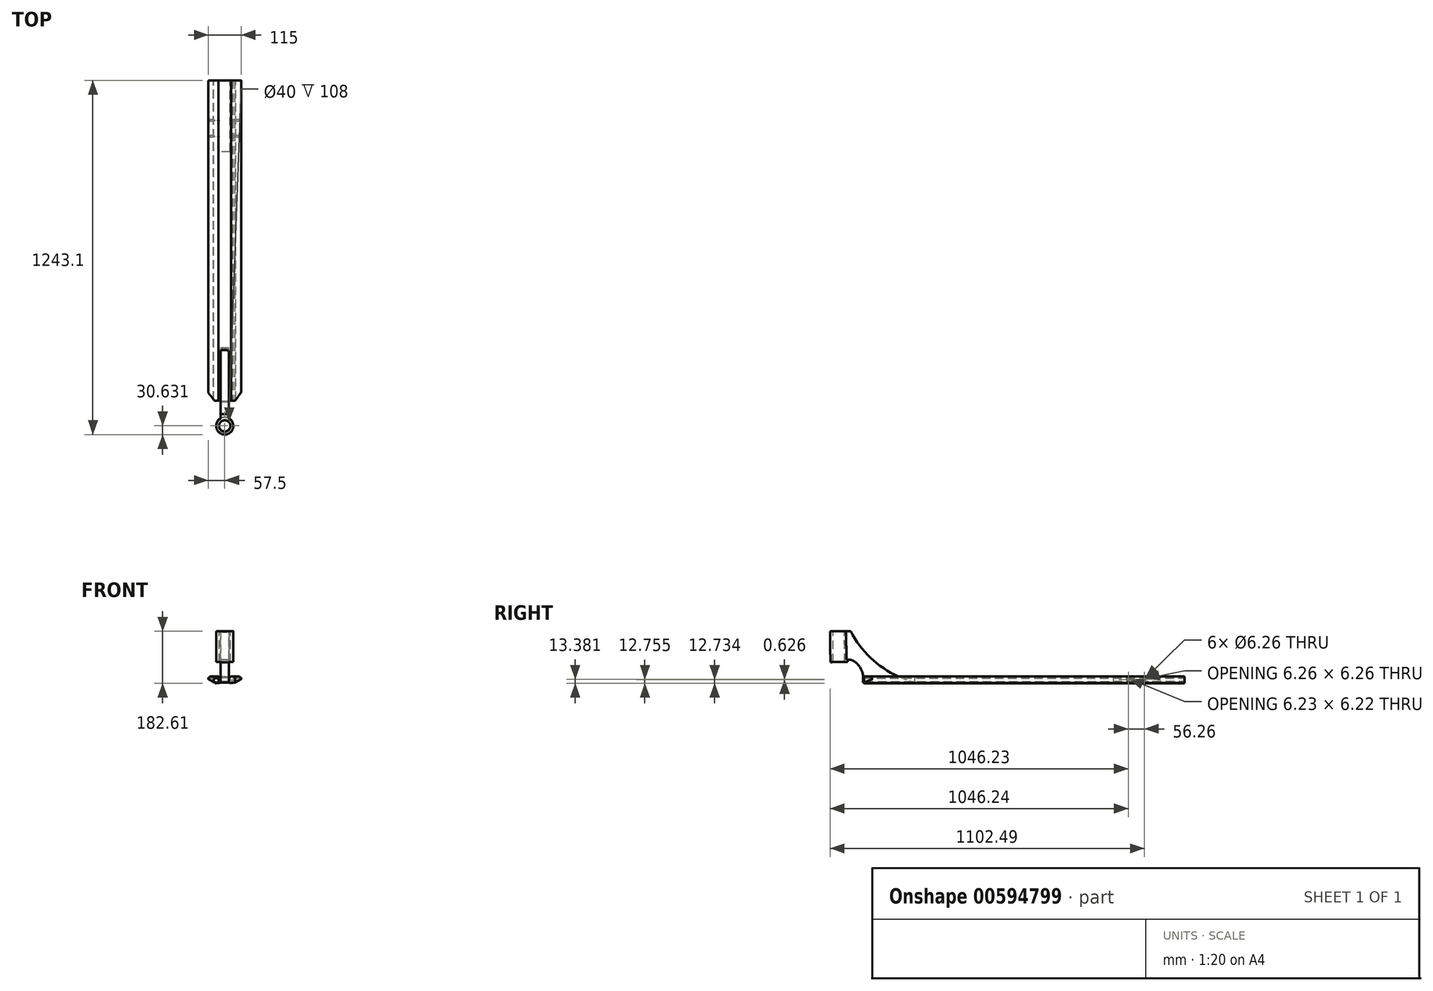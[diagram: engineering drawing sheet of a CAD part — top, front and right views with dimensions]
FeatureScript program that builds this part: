
annotation { "Feature Type Name" : "Feature", "Feature Type Description" : "" }
export const myFeature = defineFeature(function(context is Context, id is Id, definition is map)
    precondition{}
    {
        {
            var Q0;
            Q0=qCreatedBy(makeId("Front.planeOp"),FACE);
            var sketch = newSketch(context, id + "F0", { "sketchPlane" : qUnion([Q0])});
            skLineSegment(sketch, "E0", {"start": v(0, 0) * mm, "end": v(0, 33.47) * mm, "construction": true});
            skLineSegment(sketch, "E1", {"start": v(0, 25.6) * mm, "end": v(22.5, 25.6) * mm});
            skLineSegment(sketch, "E2", {"start": v(22.5, 25.6) * mm, "end": v(22.5, 26.9) * mm});
            skLineSegment(sketch, "E3", {"start": v(22.5, 26.9) * mm, "end": v(51.16, 26.9) * mm});
            skLineSegment(sketch, "E4", {"start": v(57.5, 21.58) * mm, "end": v(51.16, 26.9) * mm});
            skLineSegment(sketch, "E5", {"start": v(57.5, 21.58) * mm, "end": v(57.5, 17.58) * mm});
            skLineSegment(sketch, "E6", {"start": v(57.5, 17.58) * mm, "end": v(32.08, 2.9) * mm});
            skLineSegment(sketch, "E7.MirrorCS", {"start": v(0, 25.6) * mm, "end": v(-22.5, 25.6) * mm});
            skLineSegment(sketch, "E8.MirrorCS", {"start": v(-22.5, 25.6) * mm, "end": v(-22.5, 26.9) * mm});
            skLineSegment(sketch, "E9.MirrorCS", {"start": v(-22.5, 26.9) * mm, "end": v(-51.16, 26.9) * mm});
            skLineSegment(sketch, "E10.MirrorCS", {"start": v(-57.5, 21.58) * mm, "end": v(-51.16, 26.9) * mm});
            skLineSegment(sketch, "E11.MirrorCS", {"start": v(-57.5, 21.58) * mm, "end": v(-57.5, 17.58) * mm});
            skLineSegment(sketch, "E12.MirrorCS", {"start": v(-57.5, 17.58) * mm, "end": v(-32.08, 2.9) * mm});
            skArc(sketch, "E13", {"start": v(32.08, 2.9) * mm, "mid": v(0, 5.5) * mm, "end": v(-32.08, 2.9) * mm});
            skPoint(sketch, "E14.endSnap0", {"position": v(-57.5, 19.58) * mm});
            skSolve(sketch);
        }
        {
            var Q0;
            Q0 = qSketchRegion(id + "F0", true);
            extrude(context, id + "F1", {"entities" : qUnion([Q0]), "oppositeDirection" : true, "depth" : 931 * mm, "offsetDistance" : 25 * mm, "hasSecondDirection" : true, "secondDirectionOppositeDirection" : false, "secondDirectionDepth" : 242 * mm});
        }
        {
            var Q0;
            Q0=makeQuery(id+"F1.opExtrude","CAP_FACE",FACE,{"disambiguationData":[OSD([sQuery(id+"F0.wireOp",EDGE,"E1"),sQuery(id+"F0.wireOp",EDGE,"E2"),sQuery(id+"F0.wireOp",EDGE,"E3"),sQuery(id+"F0.wireOp",EDGE,"E4"),sQuery(id+"F0.wireOp",EDGE,"E5"),sQuery(id+"F0.wireOp",EDGE,"E6"),sQuery(id+"F0.wireOp",EDGE,"E7.MirrorCS"),sQuery(id+"F0.wireOp",EDGE,"E8.MirrorCS"),sQuery(id+"F0.wireOp",EDGE,"E9.MirrorCS"),sQuery(id+"F0.wireOp",EDGE,"E10.MirrorCS"),sQuery(id+"F0.wireOp",EDGE,"E11.MirrorCS"),sQuery(id+"F0.wireOp",EDGE,"E12.MirrorCS"),sQuery(id+"F0.wireOp",EDGE,"E13")])],"isStart":false});
            var sketch = newSketch(context, id + "F2", { "sketchPlane" : qUnion([Q0])});
            skLineSegment(sketch, "E15.bottom", {"start": v(-19, 23.6) * mm, "end": v(19, 23.6) * mm});
            skLineSegment(sketch, "E15.top", {"start": v(-19, 10.6) * mm, "end": v(19, 10.6) * mm});
            skLineSegment(sketch, "E15.left", {"start": v(-19, 23.6) * mm, "end": v(-19, 10.6) * mm});
            skLineSegment(sketch, "E15.right", {"start": v(19, 23.6) * mm, "end": v(19, 10.6) * mm});
            skSolve(sketch);
        }
        {
            var Q0;
            Q0 = qSketchRegion(id + "F2", true);
            extrude(context, id + "F3", {"entities" : qUnion([Q0]), "operationType" : NewBodyOperationType.REMOVE, "endBound" : BoundingType.SYMMETRIC, "oppositeDirection" : true, "depth" : 500 * mm, "offsetDistance" : 25 * mm});
        }
        {
            var Q0;
            Q0=makeQuery(id+"F1.opExtrude","SWEPT_EDGE",EDGE,{"disambiguationData":[OSD([sQuery(id+"F0.wireOp",EDGE,"E7.MirrorCS"),sQuery(id+"F0.wireOp",EDGE,"E8.MirrorCS")])]});
            var Q1;
            Q1=makeQuery(id+"F1.opExtrude","SWEPT_EDGE",EDGE,{"disambiguationData":[OSD([sQuery(id+"F0.wireOp",EDGE,"E1"),sQuery(id+"F0.wireOp",EDGE,"E2")])]});
            fillet(context, id + "F4", {"entities" : qUnion([Q0, Q1]), "radius" : 2 * mm, "tangentPropagation" : true, "allowEdgeOverflow" : false});
        }
        {
            var Q0;
            Q0=makeQuery(id+"F1.opExtrude","SWEPT_EDGE",EDGE,{"disambiguationData":[OSD([sQuery(id+"F0.wireOp",EDGE,"E9.MirrorCS"),sQuery(id+"F0.wireOp",EDGE,"E10.MirrorCS")])]});
            var Q1;
            Q1=makeQuery(id+"F1.opExtrude","SWEPT_EDGE",EDGE,{"disambiguationData":[OSD([sQuery(id+"F0.wireOp",EDGE,"E3"),sQuery(id+"F0.wireOp",EDGE,"E4")])]});
            var Q2;
            Q2=makeQuery(id+"F1.opExtrude","SWEPT_EDGE",EDGE,{"disambiguationData":[OSD([sQuery(id+"F0.wireOp",EDGE,"E12.MirrorCS"),sQuery(id+"F0.wireOp",EDGE,"E13")])]});
            var Q3;
            Q3=makeQuery(id+"F1.opExtrude","SWEPT_EDGE",EDGE,{"disambiguationData":[OSD([sQuery(id+"F0.wireOp",EDGE,"E6"),sQuery(id+"F0.wireOp",EDGE,"E13")])]});
            fillet(context, id + "F5", {"entities" : qUnion([Q0, Q1, Q2, Q3]), "radius" : 9 * mm, "tangentPropagation" : true, "allowEdgeOverflow" : false});
        }
        {
            var Q0;
            Q0=makeQuery(id+"F1.opExtrude","SWEPT_EDGE",EDGE,{"disambiguationData":[OSD([sQuery(id+"F0.wireOp",EDGE,"E10.MirrorCS"),sQuery(id+"F0.wireOp",EDGE,"E11.MirrorCS")])]});
            var Q1;
            Q1=makeQuery(id+"F1.opExtrude","SWEPT_EDGE",EDGE,{"disambiguationData":[OSD([sQuery(id+"F0.wireOp",EDGE,"E11.MirrorCS"),sQuery(id+"F0.wireOp",EDGE,"E12.MirrorCS")])]});
            var Q2;
            Q2=makeQuery(id+"F1.opExtrude","SWEPT_EDGE",EDGE,{"disambiguationData":[OSD([sQuery(id+"F0.wireOp",EDGE,"E4"),sQuery(id+"F0.wireOp",EDGE,"E5")])]});
            var Q3;
            Q3=makeQuery(id+"F1.opExtrude","SWEPT_EDGE",EDGE,{"disambiguationData":[OSD([sQuery(id+"F0.wireOp",EDGE,"E5"),sQuery(id+"F0.wireOp",EDGE,"E6")])]});
            fillet(context, id + "F6", {"entities" : qUnion([Q0, Q1, Q2, Q3]), "radius" : 1 * mm, "tangentPropagation" : true, "allowEdgeOverflow" : false});
        }
        {
            var Q0;
            Q0=makeQuery(id+"F1.opExtrude","CAP_FACE",FACE,{"disambiguationData":[OSD([sQuery(id+"F0.wireOp",EDGE,"E1"),sQuery(id+"F0.wireOp",EDGE,"E2"),sQuery(id+"F0.wireOp",EDGE,"E3"),sQuery(id+"F0.wireOp",EDGE,"E4"),sQuery(id+"F0.wireOp",EDGE,"E5"),sQuery(id+"F0.wireOp",EDGE,"E6"),sQuery(id+"F0.wireOp",EDGE,"E7.MirrorCS"),sQuery(id+"F0.wireOp",EDGE,"E8.MirrorCS"),sQuery(id+"F0.wireOp",EDGE,"E9.MirrorCS"),sQuery(id+"F0.wireOp",EDGE,"E10.MirrorCS"),sQuery(id+"F0.wireOp",EDGE,"E11.MirrorCS"),sQuery(id+"F0.wireOp",EDGE,"E12.MirrorCS"),sQuery(id+"F0.wireOp",EDGE,"E13")])],"isStart":false});
            var sketch = newSketch(context, id + "F7", { "sketchPlane" : qUnion([Q0])});
            skLineSegment(sketch, "E16.0.0", {"start": v(-57, 17.3) * mm, "end": v(-34.82, 4.49) * mm});
            skArc(sketch, "E16.0.1", {"start": v(-57, 17.3) * mm, "mid": v(-55.63, 18.66) * mm, "end": v(-57.5, 18.16) * mm});
            skLineSegment(sketch, "E16.0.2", {"start": v(-57.5, 21.11) * mm, "end": v(-57.5, 18.16) * mm});
            skArc(sketch, "E16.0.3", {"start": v(-57.5, 21.11) * mm, "mid": v(-55.6, 20.7) * mm, "end": v(-57.14, 21.88) * mm});
            skLineSegment(sketch, "E16.0.4", {"start": v(-53.67, 24.8) * mm, "end": v(-57.14, 21.88) * mm});
            skArc(sketch, "E16.0.5", {"start": v(-53.67, 24.8) * mm, "mid": v(-44.8, 9.45) * mm, "end": v(-47.88, 26.9) * mm});
            skLineSegment(sketch, "E16.0.6", {"start": v(-22.5, 26.9) * mm, "end": v(-47.88, 26.9) * mm});
            skArc(sketch, "E16.0.7", {"start": v(-22.5, 26.9) * mm, "mid": v(-19.49, 29.25) * mm, "end": v(-20.63, 25.6) * mm});
            skLineSegment(sketch, "E16.0.8", {"start": v(20.63, 25.6) * mm, "end": v(-20.63, 25.6) * mm});
            skArc(sketch, "E16.0.9", {"start": v(20.63, 25.6) * mm, "mid": v(19.49, 29.25) * mm, "end": v(22.5, 26.9) * mm});
            skLineSegment(sketch, "E16.0.10", {"start": v(47.88, 26.9) * mm, "end": v(22.5, 26.9) * mm});
            skArc(sketch, "E16.0.11", {"start": v(47.88, 26.9) * mm, "mid": v(44.8, 9.45) * mm, "end": v(53.67, 24.8) * mm});
            skLineSegment(sketch, "E16.0.12", {"start": v(57.14, 21.88) * mm, "end": v(53.67, 24.8) * mm});
            skArc(sketch, "E16.0.13", {"start": v(57.14, 21.88) * mm, "mid": v(55.6, 20.7) * mm, "end": v(57.5, 21.11) * mm});
            skLineSegment(sketch, "E16.0.14", {"start": v(57.5, 18.16) * mm, "end": v(57.5, 21.11) * mm});
            skArc(sketch, "E16.0.15", {"start": v(57.5, 18.16) * mm, "mid": v(55.63, 18.66) * mm, "end": v(57, 17.3) * mm});
            skLineSegment(sketch, "E16.0.16", {"start": v(34.82, 4.49) * mm, "end": v(57, 17.3) * mm});
            skArc(sketch, "E16.0.17", {"start": v(34.82, 4.49) * mm, "mid": v(28.63, 21.12) * mm, "end": v(29.02, 3.38) * mm});
            skArc(sketch, "E16.0.18", {"start": v(29.02, 3.38) * mm, "mid": v(0, -394.5) * mm, "end": v(-29.02, 3.38) * mm});
            skArc(sketch, "E16.0.19", {"start": v(-29.02, 3.38) * mm, "mid": v(-28.63, 21.12) * mm, "end": v(-34.82, 4.49) * mm});
            skArc(sketch, "E17.0", {"start": v(29.3, 5.36) * mm, "mid": v(31.64, 5.4) * mm, "end": v(33.82, 6.22) * mm});
            skArc(sketch, "E17.1", {"start": v(-29.3, 5.36) * mm, "mid": v(-24.97, 5.94) * mm, "end": v(-20.63, 6.44) * mm});
            skArc(sketch, "E17.2", {"start": v(-33.82, 6.22) * mm, "mid": v(-31.64, 5.4) * mm, "end": v(-29.3, 5.36) * mm});
            skArc(sketch, "E17.3", {"start": v(23.58, 24.9) * mm, "mid": v(22.24, 23.94) * mm, "end": v(20.63, 23.6) * mm});
            skLineSegment(sketch, "E17.4", {"start": v(35.99, 24.9) * mm, "end": v(23.58, 24.9) * mm});
            skArc(sketch, "E17.5", {"start": v(37.76, 24.68) * mm, "mid": v(36.88, 24.85) * mm, "end": v(35.99, 24.9) * mm});
            skLineSegment(sketch, "E17.6", {"start": v(52.34, 20.86) * mm, "end": v(37.76, 24.68) * mm});
            skLineSegment(sketch, "E17.7", {"start": v(20.63, 23.6) * mm, "end": v(-20.63, 23.6) * mm});
            skArc(sketch, "E17.8", {"start": v(-20.63, 23.6) * mm, "mid": v(-22.24, 23.94) * mm, "end": v(-23.58, 24.9) * mm});
            skLineSegment(sketch, "E17.9", {"start": v(-23.58, 24.9) * mm, "end": v(-35.99, 24.9) * mm});
            skLineSegment(sketch, "E17.10", {"start": v(33.82, 6.22) * mm, "end": v(52.83, 17.2) * mm});
            skArc(sketch, "E17.11", {"start": v(-35.99, 24.9) * mm, "mid": v(-36.88, 24.85) * mm, "end": v(-37.76, 24.68) * mm});
            skLineSegment(sketch, "E17.12", {"start": v(-37.76, 24.68) * mm, "end": v(-52.34, 20.86) * mm});
            skLineSegment(sketch, "E17.13", {"start": v(-52.83, 17.2) * mm, "end": v(-33.82, 6.22) * mm});
            skPoint(sketch, "E18.visualSharp", {"position": v(-57.05, 19.63) * mm});
            skArc(sketch, "E18.filletArc", {"start": v(-52.34, 20.86) * mm, "mid": v(-53.82, 19.2) * mm, "end": v(-52.83, 17.2) * mm});
            skPoint(sketch, "E19.visualSharp", {"position": v(57.05, 19.63) * mm});
            skArc(sketch, "E19.filletArc", {"start": v(52.83, 17.2) * mm, "mid": v(53.82, 19.2) * mm, "end": v(52.34, 20.86) * mm});
            skLineSegment(sketch, "E20", {"start": v(-20.63, 23.6) * mm, "end": v(-20.63, 6.44) * mm});
            skLineSegment(sketch, "E21", {"start": v(20.63, 23.6) * mm, "end": v(20.63, 6.44) * mm});
            skArc(sketch, "E22.trimOffspring", {"start": v(20.63, 6.44) * mm, "mid": v(24.97, 5.94) * mm, "end": v(29.3, 5.36) * mm});
            skSolve(sketch);
        }
        {
            var Q0;
            Q0=makeQuery(id+"F7.imprint","IMPRINT",FACE,{"disambiguationData":[TD([[makeQuery(id+"F7.imprint","IMPRINT",EDGE,{"derivedFrom":sQuery(id+"F7.wireOp",EDGE,"E17.1")}),1.0]])]});
            var Q1;
            Q1=makeQuery(id+"F7.imprint","IMPRINT",FACE,{"disambiguationData":[TD([[makeQuery(id+"F7.imprint","IMPRINT",EDGE,{"derivedFrom":sQuery(id+"F7.wireOp",EDGE,"E17.0")}),1.0]])]});
            extrude(context, id + "F8", {"entities" : qUnion([Q0, Q1]), "operationType" : NewBodyOperationType.REMOVE, "endBound" : BoundingType.THROUGH_ALL, "oppositeDirection" : true, "depth" : 25 * mm, "offsetDistance" : 25 * mm});
        }
        {
            var Q0;
            Q0=makeQuery(id+"F1.opExtrude","SWEPT_FACE",FACE,{"disambiguationData":[OSD([sQuery(id+"F0.wireOp",EDGE,"E1"),sQuery(id+"F0.wireOp",EDGE,"E7.MirrorCS")])]});
            var sketch = newSketch(context, id + "F9", { "sketchPlane" : qUnion([Q0])});
            skArc(sketch, "E23", {"start": v(57.5, -292.2) * mm, "mid": v(0.1, -234.5) * mm, "end": v(-57.5, -292) * mm});
            skLineSegment(sketch, "E24", {"start": v(-57.5, -292) * mm, "end": v(-57.5, -212.2) * mm});
            skLineSegment(sketch, "E25", {"start": v(-57.5, -212.2) * mm, "end": v(57.77, -212.2) * mm});
            skLineSegment(sketch, "E26", {"start": v(57.77, -212.2) * mm, "end": v(57.5, -292.2) * mm});
            skSolve(sketch);
        }
        {
            var Q0;
            Q0 = qSketchRegion(id + "F9", true);
            extrude(context, id + "F10", {"entities" : qUnion([Q0]), "operationType" : NewBodyOperationType.REMOVE, "endBound" : BoundingType.THROUGH_ALL, "oppositeDirection" : true, "depth" : 25 * mm, "offsetDistance" : 25 * mm});
        }
        {
            var Q0;
            Q0=qCreatedBy(makeId("Top.planeOp"),FACE);
            var sketch = newSketch(context, id + "F11", { "sketchPlane" : qUnion([Q0])});
            skLineSegment(sketch, "E27", {"start": v(-68.2, -250) * mm, "end": v(67.8, -250) * mm});
            skLineSegment(sketch, "E28", {"start": v(67.8, -250) * mm, "end": v(67.8, -150) * mm});
            skLineSegment(sketch, "E29", {"start": v(67.8, -150) * mm, "end": v(36.07, -193.68) * mm});
            skLineSegment(sketch, "E30", {"start": v(36.07, -193.68) * mm, "end": v(15.09, -193.68) * mm});
            skLineSegment(sketch, "E31", {"start": v(15.09, -193.68) * mm, "end": v(15.09, -16) * mm});
            skLineSegment(sketch, "E32", {"start": v(15.09, -16) * mm, "end": v(-16.91, -16) * mm});
            skLineSegment(sketch, "E33", {"start": v(-16.91, -16) * mm, "end": v(-16.91, -193.68) * mm});
            skLineSegment(sketch, "E34", {"start": v(-16.91, -193.68) * mm, "end": v(-36.45, -193.68) * mm});
            skLineSegment(sketch, "E35", {"start": v(-36.45, -193.68) * mm, "end": v(-68.2, -150) * mm});
            skLineSegment(sketch, "E36", {"start": v(-68.2, -150) * mm, "end": v(-68.2, -250) * mm});
            skSolve(sketch);
        }
        {
            var Q0;
            Q0 = qSketchRegion(id + "F11", true);
            extrude(context, id + "F12", {"entities" : qUnion([Q0]), "operationType" : NewBodyOperationType.REMOVE, "endBound" : BoundingType.THROUGH_ALL, "depth" : 27 * mm, "offsetDistance" : 25 * mm});
        }
        {
            var Q0;
            {var subQ0=sQuery(id+"F11.wireOp",EDGE,"E32");var subQ1=sQuery(id+"F11.wireOp",EDGE,"E33");Q0=makeQuery(id+"F12.boolean.opBoolean","COPY",EDGE,{"disambiguationData":[TD([makeQuery(id+"F3.boolean.opBoolean","COPY",FACE,{"derivedFrom":makeQuery(id+"F3.opExtrude","SWEPT_FACE",FACE,{"disambiguationData":[OSD([sQuery(id+"F2.wireOp",EDGE,"E15.bottom")])]})})])],"derivedFrom":makeQuery(id+"F12.opExtrude","SWEPT_EDGE",EDGE,{"disambiguationData":[OSD([subQ0,subQ1])]})});}
            var Q1;
            {var subQ0=sQuery(id+"F11.wireOp",EDGE,"E31");var subQ1=sQuery(id+"F11.wireOp",EDGE,"E32");Q1=makeQuery(id+"F12.boolean.opBoolean","COPY",EDGE,{"disambiguationData":[TD([makeQuery(id+"F3.boolean.opBoolean","COPY",FACE,{"derivedFrom":makeQuery(id+"F3.opExtrude","SWEPT_FACE",FACE,{"disambiguationData":[OSD([sQuery(id+"F2.wireOp",EDGE,"E15.bottom")])]})})])],"derivedFrom":makeQuery(id+"F12.opExtrude","SWEPT_EDGE",EDGE,{"disambiguationData":[OSD([subQ0,subQ1])]})});}
            var Q2;
            {var subQ0=sQuery(id+"F11.wireOp",EDGE,"E34");var subQ1=sQuery(id+"F11.wireOp",EDGE,"E33");Q2=makeQuery(id+"F12.boolean.opBoolean","COPY",EDGE,{"disambiguationData":[TD([makeQuery(id+"F3.boolean.opBoolean","COPY",FACE,{"derivedFrom":makeQuery(id+"F3.opExtrude","SWEPT_FACE",FACE,{"disambiguationData":[OSD([sQuery(id+"F2.wireOp",EDGE,"E15.bottom")])]})})])],"derivedFrom":makeQuery(id+"F12.opExtrude","SWEPT_EDGE",EDGE,{"disambiguationData":[OSD([subQ1,subQ0])]})});}
            var Q3;
            {var subQ0=sQuery(id+"F11.wireOp",EDGE,"E31");var subQ1=sQuery(id+"F11.wireOp",EDGE,"E30");Q3=makeQuery(id+"F12.boolean.opBoolean","COPY",EDGE,{"disambiguationData":[TD([makeQuery(id+"F3.boolean.opBoolean","COPY",FACE,{"derivedFrom":makeQuery(id+"F3.opExtrude","SWEPT_FACE",FACE,{"disambiguationData":[OSD([sQuery(id+"F2.wireOp",EDGE,"E15.bottom")])]})})])],"derivedFrom":makeQuery(id+"F12.opExtrude","SWEPT_EDGE",EDGE,{"disambiguationData":[OSD([subQ1,subQ0])]})});}
            var Q4;
            {var subQ0=sQuery(id+"F11.wireOp",EDGE,"E33");var subQ1=sQuery(id+"F11.wireOp",EDGE,"E32");Q4=makeQuery(id+"F12.boolean.opBoolean","COPY",EDGE,{"disambiguationData":[TD([makeQuery(id+"F1.opExtrude","SWEPT_FACE",FACE,{"disambiguationData":[OSD([sQuery(id+"F0.wireOp",EDGE,"E13")])]})])],"derivedFrom":makeQuery(id+"F12.opExtrude","SWEPT_EDGE",EDGE,{"disambiguationData":[OSD([subQ1,subQ0])]})});}
            var Q5;
            {var subQ0=sQuery(id+"F11.wireOp",EDGE,"E31");var subQ1=sQuery(id+"F11.wireOp",EDGE,"E32");Q5=makeQuery(id+"F12.boolean.opBoolean","COPY",EDGE,{"disambiguationData":[TD([makeQuery(id+"F1.opExtrude","SWEPT_FACE",FACE,{"disambiguationData":[OSD([sQuery(id+"F0.wireOp",EDGE,"E13")])]})])],"derivedFrom":makeQuery(id+"F12.opExtrude","SWEPT_EDGE",EDGE,{"disambiguationData":[OSD([subQ0,subQ1])]})});}
            fillet(context, id + "F13", {"entities" : qUnion([Q0, Q1, Q2, Q3, Q4, Q5]), "radius" : 7.73 * mm, "tangentPropagation" : true, "allowEdgeOverflow" : false});
        }
        {
            var Q0;
            Q0=makeQuery(id+"F3.boolean.opBoolean","COPY",FACE,{"derivedFrom":makeQuery(id+"F3.opExtrude","SWEPT_FACE",FACE,{"disambiguationData":[OSD([sQuery(id+"F2.wireOp",EDGE,"E15.right")])]})});
            var sketch = newSketch(context, id + "F14", { "sketchPlane" : qUnion([Q0])});
            skCircle(sketch, "E37", {"center": v(790.4, 16.66) * mm, "radius": 3.13 * mm});
            skCircle(sketch, "E38", {"center": v(734.13, 16.04) * mm, "radius": 3.13 * mm});
            skSolve(sketch);
        }
        {
            var Q0;
            Q0 = qSketchRegion(id + "F14", true);
            extrude(context, id + "F15", {"entities" : qUnion([Q0]), "operationType" : NewBodyOperationType.REMOVE, "depth" : 89 * mm, "offsetDistance" : 25 * mm, "hasSecondDirection" : true, "secondDirectionOppositeDirection" : true, "secondDirectionDepth" : 62 * mm});
        }
        {
            var Q0;
            Q0=qCreatedBy(makeId("Right.planeOp"),FACE);
            var sketch = newSketch(context, id + "F16", { "sketchPlane" : qUnion([Q0])});
            skLineSegment(sketch, "E39", {"start": v(-8.1, 5) * mm, "end": v(-198.1, 5) * mm});
            skArc(sketch, "E40", {"start": v(-198.1, 5) * mm, "mid": v(-203.66, 52.95) * mm, "end": v(-238.95, 85.9) * mm});
            skLineSegment(sketch, "E41", {"start": v(-238.95, 85.9) * mm, "end": v(-284.95, 85.4) * mm});
            skLineSegment(sketch, "E42", {"start": v(-284.95, 85.4) * mm, "end": v(-286.05, 185.39) * mm});
            skLineSegment(sketch, "E43", {"start": v(-286.05, 185.39) * mm, "end": v(-240.05, 185.89) * mm});
            skArc(sketch, "E44", {"start": v(-240.05, 185.89) * mm, "mid": v(-144, 69.9) * mm, "end": v(-8.1, 5) * mm});
            skSolve(sketch);
        }
        {
            var Q0;
            Q0 = qSketchRegion(id + "F16", true);
            extrude(context, id + "F17", {"entities" : qUnion([Q0]), "operationType" : NewBodyOperationType.ADD, "endBound" : BoundingType.SYMMETRIC, "depth" : 30 * mm, "offsetDistance" : 25 * mm});
        }
        {
            var Q0;
            Q0=makeQuery(id+"F17.opExtrude","SWEPT_FACE",FACE,{"disambiguationData":[OSD([sQuery(id+"F16.wireOp",EDGE,"E43")])]});
            var sketch = newSketch(context, id + "F18", { "sketchPlane" : qUnion([Q0])});
            skCircle(sketch, "E45", {"center": v(0, -280.06) * mm, "radius": 30 * mm});
            skSolve(sketch);
        }
        {
            var Q0;
            {var subQ1=sQuery(id+"F16.wireOp",EDGE,"E43");var subQ6=makeQuery(id+"F17.opExtrude","SWEPT_EDGE",EDGE,{"disambiguationData":[OSD([sQuery(id+"F16.wireOp",EDGE,"E42"),subQ1])]});Q0=makeQuery(id+"F18.imprint","IMPRINT",FACE,{"disambiguationData":[TD([[makeQuery(id+"F18.imprint","IMPRINT",EDGE,{"derivedFrom":subQ6}),-1.0]])]});}
            var Q1;
            {var subQ1=sQuery(id+"F16.wireOp",EDGE,"E43");var subQ6=makeQuery(id+"F17.opExtrude","SWEPT_EDGE",EDGE,{"disambiguationData":[OSD([sQuery(id+"F16.wireOp",EDGE,"E42"),subQ1])]});Q1=makeQuery(id+"F18.imprint","IMPRINT",FACE,{"disambiguationData":[TD([[makeQuery(id+"F18.imprint","IMPRINT",EDGE,{"derivedFrom":subQ6}),1.0]])]});}
            extrude(context, id + "F19", {"entities" : qUnion([Q0, Q1]), "operationType" : NewBodyOperationType.ADD, "oppositeDirection" : true, "depth" : 108 * mm, "offsetDistance" : 25 * mm});
        }
        {
            var Q0;
            Q0=makeQuery(id+"F19.boolean.opBoolean","MERGE",FACE,{"derivedFrom":[makeQuery(id+"F17.opExtrude","SWEPT_FACE",FACE,{"disambiguationData":[OSD([sQuery(id+"F16.wireOp",EDGE,"E43")])]}),makeQuery(id+"F19.opExtrude","CAP_FACE",FACE,{"disambiguationData":[OSD([sQuery(id+"F18.wireOp",EDGE,"E45")])],"isStart":true})]});
            var sketch = newSketch(context, id + "F20", { "sketchPlane" : qUnion([Q0])});
            skPoint(sketch, "E46", {"position": v(0, -280.06) * mm});
            skSolve(sketch);
        }
        {
            var Q0;
            Q0=sQuery(id+"F20.wireOp",VERTEX,"E46");
            var Q1;
            Q1=makeQuery(id+"F1.opExtrude","SWEPT_BODY",BODY,{"disambiguationData":[OSD([sQuery(id+"F0.wireOp",EDGE,"E1"),sQuery(id+"F0.wireOp",EDGE,"E2"),sQuery(id+"F0.wireOp",EDGE,"E3"),sQuery(id+"F0.wireOp",EDGE,"E4"),sQuery(id+"F0.wireOp",EDGE,"E5"),sQuery(id+"F0.wireOp",EDGE,"E6"),sQuery(id+"F0.wireOp",EDGE,"E7.MirrorCS"),sQuery(id+"F0.wireOp",EDGE,"E8.MirrorCS"),sQuery(id+"F0.wireOp",EDGE,"E9.MirrorCS"),sQuery(id+"F0.wireOp",EDGE,"E10.MirrorCS"),sQuery(id+"F0.wireOp",EDGE,"E11.MirrorCS"),sQuery(id+"F0.wireOp",EDGE,"E12.MirrorCS"),sQuery(id+"F0.wireOp",EDGE,"E13")])]});
            hole(context, id + "F21", {"style" : HoleStyle.SIMPLE, "endStyle" : HoleEndStyle.THROUGH, "holeDiameter" : 40 * mm, "majorDiameter" : 5 * mm, "isTappedThrough" : true, "tappedDepth" : 12 * mm, "tapClearance" : 3, "locations" : qUnion([Q0]), "scope" : qUnion([Q1])});
        }
    });
